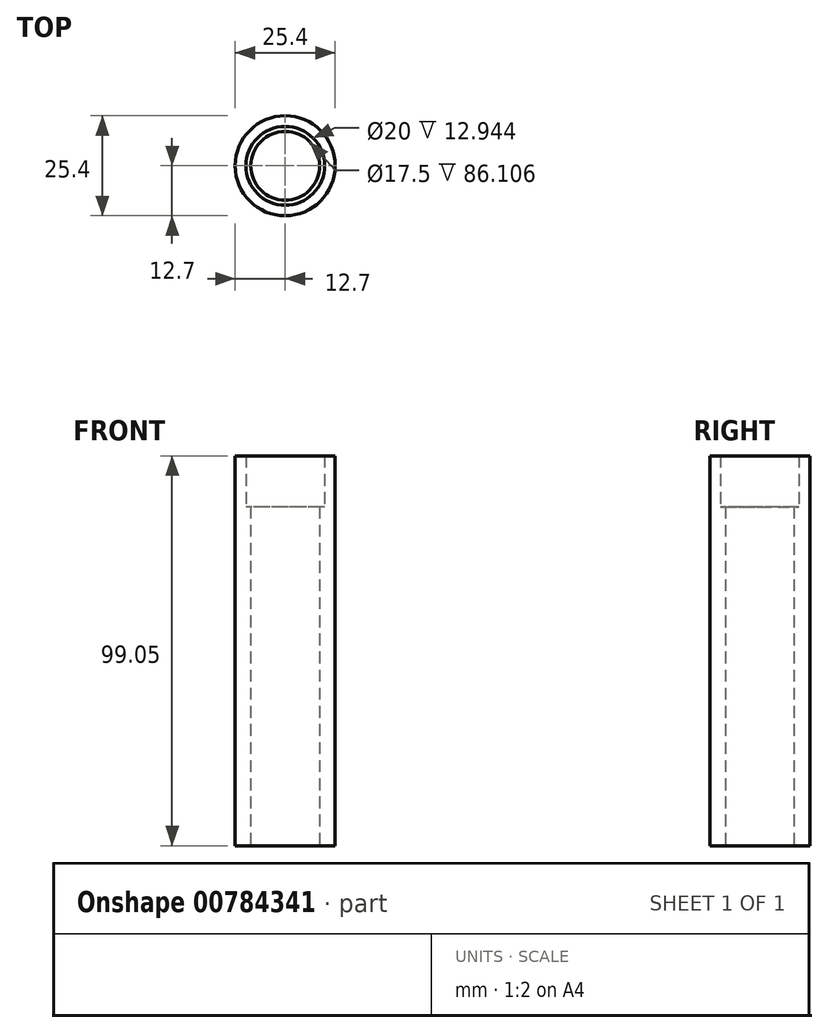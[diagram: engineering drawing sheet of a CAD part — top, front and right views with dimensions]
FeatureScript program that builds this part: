
annotation { "Feature Type Name" : "Feature", "Feature Type Description" : "" }
export const myFeature = defineFeature(function(context is Context, id is Id, definition is map)
    precondition{}
    {
        {
            var Q0;
            Q0=qCreatedBy(makeId("Top.planeOp"),FACE);
            var sketch = newSketch(context, id + "F0", { "sketchPlane" : qUnion([Q0])});
            skCircle(sketch, "E0", {"center": v(0, 0) * mm, "radius": 10 * mm});
            skCircle(sketch, "E1", {"center": v(0, 0) * mm, "radius": 12.7 * mm});
            skSolve(sketch);
        }
        {
            var Q0;
            Q0=makeQuery(id+"F0.imprint","IMPRINT",FACE,{"disambiguationData":[TD([[makeQuery(id+"F0.imprint","IMPRINT",EDGE,{"derivedFrom":sQuery(id+"F0.wireOp",EDGE,"E0")}),-1.0]])]});
            extrude(context, id + "F1", {"entities" : qUnion([Q0]), "depth" : 80 * mm, "offsetDistance" : 25.4 * mm});
        }
        {
            var Q0;
            Q0=qCreatedBy(makeId("Top.planeOp"),FACE);
            var sketch = newSketch(context, id + "F2", { "sketchPlane" : qUnion([Q0])});
            skCircle(sketch, "E2", {"center": v(0, 0) * mm, "radius": 10 * mm});
            skCircle(sketch, "E3", {"center": v(0, 0) * mm, "radius": 8.75 * mm});
            skSolve(sketch);
        }
        {
            var Q0;
            Q0=makeQuery(id+"F2.imprint","IMPRINT",FACE,{"disambiguationData":[TD([[makeQuery(id+"F2.imprint","IMPRINT",EDGE,{"derivedFrom":sQuery(id+"F2.wireOp",EDGE,"E2")}),1.0]])]});
            extrude(context, id + "F3", {"entities" : qUnion([Q0]), "operationType" : NewBodyOperationType.ADD, "depth" : 67.06 * mm, "offsetDistance" : 25.4 * mm});
        }
        {
            var Q0;
            Q0=makeQuery(id+"F3.boolean.opBoolean","MERGE",FACE,{"derivedFrom":[makeQuery(id+"F1.opExtrude","CAP_FACE",FACE,{"disambiguationData":[OSD([sQuery(id+"F0.wireOp",EDGE,"E0"),sQuery(id+"F0.wireOp",EDGE,"E1")])],"isStart":true}),makeQuery(id+"F3.opExtrude","CAP_FACE",FACE,{"disambiguationData":[OSD([sQuery(id+"F2.wireOp",EDGE,"E2"),sQuery(id+"F2.wireOp",EDGE,"E3")])],"isStart":true})]});
            extrude(context, id + "F4", {"entities" : qUnion([Q0]), "operationType" : NewBodyOperationType.ADD, "depth" : 19.05 * mm, "offsetDistance" : 25.4 * mm});
        }
    });
